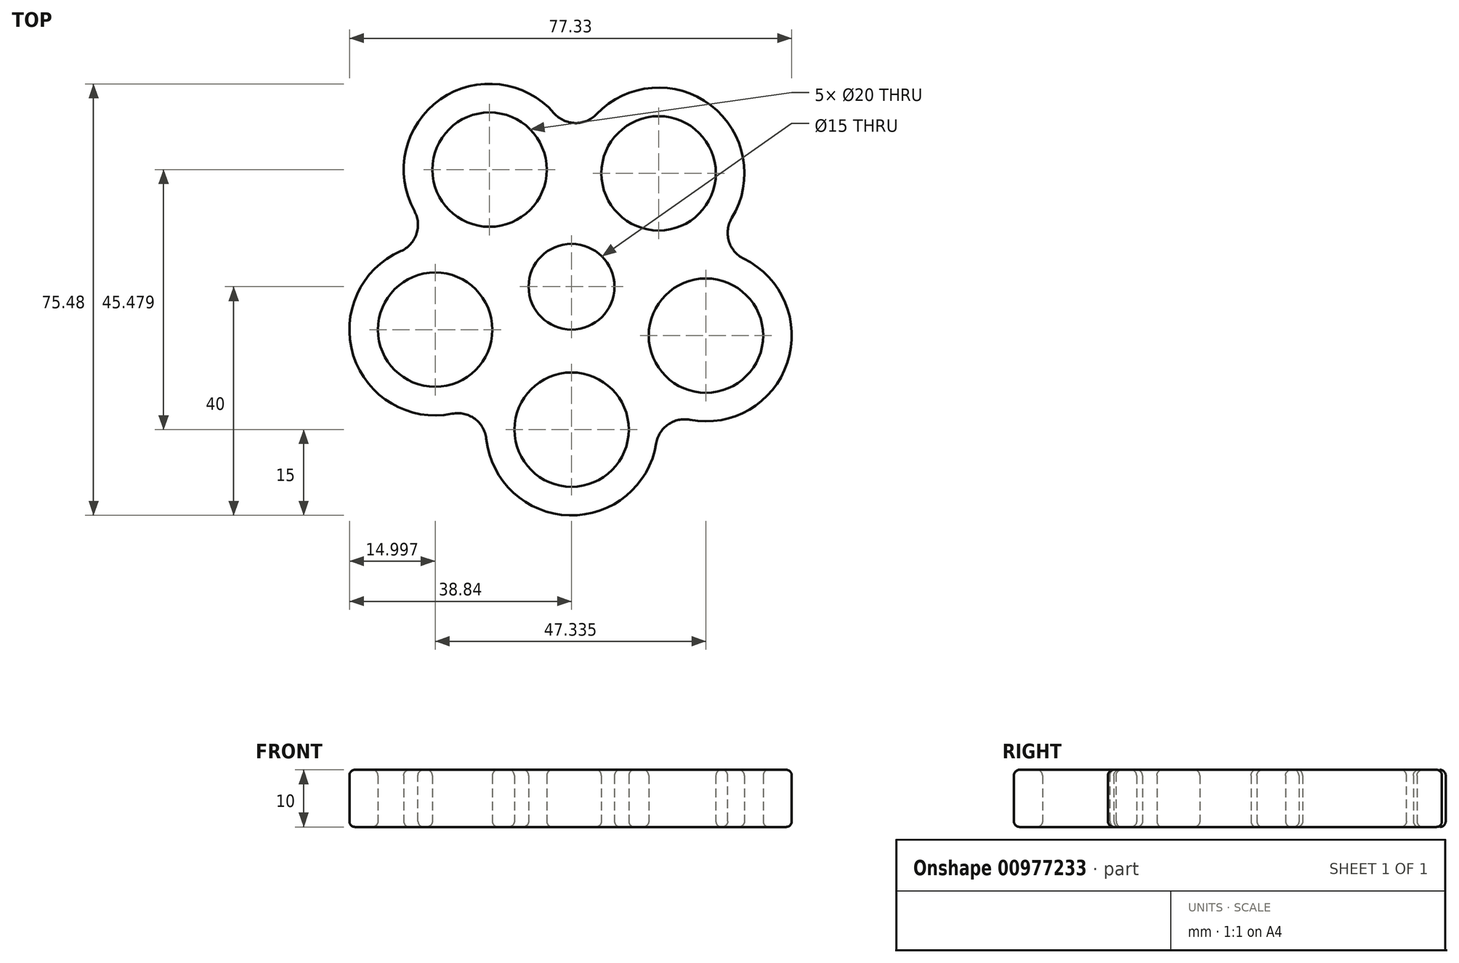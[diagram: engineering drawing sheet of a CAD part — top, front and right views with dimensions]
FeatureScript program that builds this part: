
annotation { "Feature Type Name" : "Feature", "Feature Type Description" : "" }
export const myFeature = defineFeature(function(context is Context, id is Id, definition is map)
    precondition{}
    {
        {
            var Q0;
            Q0=qCreatedBy(makeId("Top.planeOp"),FACE);
            var sketch = newSketch(context, id + "F0", { "sketchPlane" : qUnion([Q0])});
            skCircle(sketch, "E0", {"center": v(0, 0) * mm, "radius": 7.5 * mm});
            skCircle(sketch, "E1", {"center": v(0, 0) * mm, "radius": 15 * mm});
            skCircle(sketch, "E2", {"center": v(0, -25) * mm, "radius": 10 * mm});
            skCircle(sketch, "E3", {"center": v(0, -25) * mm, "radius": 15 * mm});
            skCircle(sketch, "E4.1.0", {"center": v(-23.84, -7.52) * mm, "radius": 15 * mm});
            skCircle(sketch, "E4.1.1", {"center": v(-23.84, -7.52) * mm, "radius": 10 * mm});
            skCircle(sketch, "E4.2.0", {"center": v(-14.34, 20.48) * mm, "radius": 15 * mm});
            skCircle(sketch, "E4.2.1", {"center": v(-14.34, 20.48) * mm, "radius": 10 * mm});
            skCircle(sketch, "E4.3.0", {"center": v(15.22, 19.83) * mm, "radius": 15 * mm});
            skCircle(sketch, "E4.3.1", {"center": v(15.22, 19.83) * mm, "radius": 10 * mm});
            skCircle(sketch, "E4.4.0", {"center": v(23.5, -8.55) * mm, "radius": 15 * mm});
            skCircle(sketch, "E4.4.1", {"center": v(23.5, -8.55) * mm, "radius": 10 * mm});
            skSolve(sketch);
        }
        {
            var Q0;
            Q0 = qSketchRegion(id + "F0", true);
            var Q1;
            {var subQ0=sQuery(id+"F0.wireOp",EDGE,"E1");var subQ1=makeQuery(id+"F0.imprint","INTERSECT",VERTEX,{"derivedFrom":[subQ0,sQuery(id+"F0.wireOp",EDGE,"E4.2.1")]});Q1=makeQuery(id+"F0.imprint","IMPRINT",FACE,{"disambiguationData":[TD([[makeQuery(id+"F0.imprint","IMPRINT",EDGE,{"disambiguationData":[TD([[subQ1,1.0]])],"derivedFrom":subQ0}),1.0]])]});}
            var Q2;
            {var subQ0=sQuery(id+"F0.wireOp",EDGE,"E1");var subQ1=makeQuery(id+"F0.imprint","INTERSECT",VERTEX,{"derivedFrom":[subQ0,sQuery(id+"F0.wireOp",EDGE,"E4.1.1")]});Q2=makeQuery(id+"F0.imprint","IMPRINT",FACE,{"disambiguationData":[TD([[makeQuery(id+"F0.imprint","IMPRINT",EDGE,{"disambiguationData":[TD([[subQ1,1.0]])],"derivedFrom":subQ0}),1.0]])]});}
            var Q3;
            Q3=makeQuery(id+"F0.imprint","IMPRINT",FACE,{"disambiguationData":[TD([[makeQuery(id+"F0.imprint","IMPRINT",EDGE,{"derivedFrom":sQuery(id+"F0.wireOp",EDGE,"E0")}),-1.0]])]});
            var Q4;
            {var subQ0=sQuery(id+"F0.wireOp",EDGE,"E1");var subQ1=makeQuery(id+"F0.imprint","INTERSECT",VERTEX,{"derivedFrom":[subQ0,sQuery(id+"F0.wireOp",EDGE,"E2")]});Q4=makeQuery(id+"F0.imprint","IMPRINT",FACE,{"disambiguationData":[TD([[makeQuery(id+"F0.imprint","IMPRINT",EDGE,{"disambiguationData":[TD([[subQ1,1.0]])],"derivedFrom":subQ0}),1.0]])]});}
            var Q5;
            {var subQ0=sQuery(id+"F0.wireOp",EDGE,"E1");var subQ1=makeQuery(id+"F0.imprint","INTERSECT",VERTEX,{"derivedFrom":[subQ0,sQuery(id+"F0.wireOp",EDGE,"E4.4.1")]});Q5=makeQuery(id+"F0.imprint","IMPRINT",FACE,{"disambiguationData":[TD([[makeQuery(id+"F0.imprint","IMPRINT",EDGE,{"disambiguationData":[TD([[subQ1,1.0]])],"derivedFrom":subQ0}),1.0]])]});}
            var Q6;
            {var subQ0=sQuery(id+"F0.wireOp",EDGE,"E1");var subQ1=makeQuery(id+"F0.imprint","INTERSECT",VERTEX,{"derivedFrom":[subQ0,sQuery(id+"F0.wireOp",EDGE,"E4.3.1")]});Q6=makeQuery(id+"F0.imprint","IMPRINT",FACE,{"disambiguationData":[TD([[makeQuery(id+"F0.imprint","IMPRINT",EDGE,{"disambiguationData":[TD([[subQ1,1.0]])],"derivedFrom":subQ0}),1.0]])]});}
            var Q7;
            {var subQ0=sQuery(id+"F0.wireOp",EDGE,"E4.3.0");var subQ1=sQuery(id+"F0.wireOp",EDGE,"E1");var subQ2=makeQuery(id+"F0.imprint","INTERSECT",VERTEX,{"disambiguationData":[OD(0.0)],"derivedFrom":[subQ1,subQ0]});Q7=makeQuery(id+"F0.imprint","IMPRINT",FACE,{"disambiguationData":[TD([[makeQuery(id+"F0.imprint","IMPRINT",EDGE,{"disambiguationData":[TD([[subQ2,1.0]])],"derivedFrom":subQ1}),-1.0]])]});}
            var Q8;
            {var subQ0=sQuery(id+"F0.wireOp",EDGE,"E4.3.0");var subQ1=sQuery(id+"F0.wireOp",EDGE,"E1");var subQ2=makeQuery(id+"F0.imprint","INTERSECT",VERTEX,{"disambiguationData":[OD(1.0)],"derivedFrom":[subQ1,subQ0]});Q8=makeQuery(id+"F0.imprint","IMPRINT",FACE,{"disambiguationData":[TD([[makeQuery(id+"F0.imprint","IMPRINT",EDGE,{"disambiguationData":[TD([[subQ2,-1.0]])],"derivedFrom":subQ1}),-1.0]])]});}
            var Q9;
            {var subQ0=sQuery(id+"F0.wireOp",EDGE,"E4.2.0");var subQ1=sQuery(id+"F0.wireOp",EDGE,"E1");var subQ2=makeQuery(id+"F0.imprint","INTERSECT",VERTEX,{"disambiguationData":[OD(1.0)],"derivedFrom":[subQ1,subQ0]});Q9=makeQuery(id+"F0.imprint","IMPRINT",FACE,{"disambiguationData":[TD([[makeQuery(id+"F0.imprint","IMPRINT",EDGE,{"disambiguationData":[TD([[subQ2,-1.0]])],"derivedFrom":subQ1}),-1.0]])]});}
            var Q10;
            {var subQ0=sQuery(id+"F0.wireOp",EDGE,"E4.1.0");var subQ1=sQuery(id+"F0.wireOp",EDGE,"E1");var subQ2=makeQuery(id+"F0.imprint","INTERSECT",VERTEX,{"disambiguationData":[OD(1.0)],"derivedFrom":[subQ1,subQ0]});Q10=makeQuery(id+"F0.imprint","IMPRINT",FACE,{"disambiguationData":[TD([[makeQuery(id+"F0.imprint","IMPRINT",EDGE,{"disambiguationData":[TD([[subQ2,-1.0]])],"derivedFrom":subQ1}),-1.0]])]});}
            var Q11;
            {var subQ0=sQuery(id+"F0.wireOp",EDGE,"E3");var subQ1=sQuery(id+"F0.wireOp",EDGE,"E1");var subQ2=makeQuery(id+"F0.imprint","INTERSECT",VERTEX,{"disambiguationData":[OD(1.0)],"derivedFrom":[subQ1,subQ0]});Q11=makeQuery(id+"F0.imprint","IMPRINT",FACE,{"disambiguationData":[TD([[makeQuery(id+"F0.imprint","IMPRINT",EDGE,{"disambiguationData":[TD([[subQ2,-1.0]])],"derivedFrom":subQ1}),-1.0]])]});}
            extrude(context, id + "F1", {"entities" : qUnion([Q0, Q1, Q2, Q3, Q4, Q5, Q6, Q7, Q8, Q9, Q10, Q11]), "depth" : 10 * mm, "offsetDistance" : 25 * mm});
        }
        {
            var Q0;
            Q0=makeQuery(id+"F1.opExtrude","SWEPT_EDGE",EDGE,{"disambiguationData":[OSD([sQuery(id+"F0.wireOp",EDGE,"E3"),sQuery(id+"F0.wireOp",EDGE,"E4.4.0")])]});
            var Q1;
            Q1=makeQuery(id+"F1.opExtrude","SWEPT_EDGE",EDGE,{"disambiguationData":[OSD([sQuery(id+"F0.wireOp",EDGE,"E4.3.0"),sQuery(id+"F0.wireOp",EDGE,"E4.4.0")])]});
            var Q2;
            Q2=makeQuery(id+"F1.opExtrude","SWEPT_EDGE",EDGE,{"disambiguationData":[OSD([sQuery(id+"F0.wireOp",EDGE,"E4.2.0"),sQuery(id+"F0.wireOp",EDGE,"E4.3.0")])]});
            var Q3;
            Q3=makeQuery(id+"F1.opExtrude","SWEPT_EDGE",EDGE,{"disambiguationData":[OSD([sQuery(id+"F0.wireOp",EDGE,"E4.1.0"),sQuery(id+"F0.wireOp",EDGE,"E4.2.0")])]});
            var Q4;
            Q4=makeQuery(id+"F1.opExtrude","SWEPT_EDGE",EDGE,{"disambiguationData":[OSD([sQuery(id+"F0.wireOp",EDGE,"E3"),sQuery(id+"F0.wireOp",EDGE,"E4.1.0")])]});
            fillet(context, id + "F2", {"entities" : qUnion([Q0, Q1, Q2, Q3, Q4]), "radius" : 5 * mm, "tangentPropagation" : true, "allowEdgeOverflow" : false});
        }
        {
            var Q0;
            {var subQ0=sQuery(id+"F0.wireOp",EDGE,"E4.2.0");var subQ1=sQuery(id+"F0.wireOp",EDGE,"E4.1.0");Q0=makeQuery(id+"F2.opFillet","BLEND_EDGE",EDGE,{"blendedFrom":[makeQuery(id+"F1.opExtrude","SWEPT_EDGE",EDGE,{"disambiguationData":[OSD([subQ1,subQ0])]}),makeQuery(id+"F1.opExtrude","CAP_FACE",FACE,{"disambiguationData":[OSD([sQuery(id+"F0.wireOp",EDGE,"E0"),sQuery(id+"F0.wireOp",EDGE,"E2"),sQuery(id+"F0.wireOp",EDGE,"E3"),subQ1,sQuery(id+"F0.wireOp",EDGE,"E4.1.1"),subQ0,sQuery(id+"F0.wireOp",EDGE,"E4.2.1"),sQuery(id+"F0.wireOp",EDGE,"E4.3.0"),sQuery(id+"F0.wireOp",EDGE,"E4.3.1"),sQuery(id+"F0.wireOp",EDGE,"E4.4.0"),sQuery(id+"F0.wireOp",EDGE,"E4.4.1")])],"isStart":true})],"blendedInto":[makeQuery(id+"F1.opExtrude","CAP_FACE",FACE,{"disambiguationData":[OSD([sQuery(id+"F0.wireOp",EDGE,"E0"),sQuery(id+"F0.wireOp",EDGE,"E2"),sQuery(id+"F0.wireOp",EDGE,"E3"),subQ1,sQuery(id+"F0.wireOp",EDGE,"E4.1.1"),subQ0,sQuery(id+"F0.wireOp",EDGE,"E4.2.1"),sQuery(id+"F0.wireOp",EDGE,"E4.3.0"),sQuery(id+"F0.wireOp",EDGE,"E4.3.1"),sQuery(id+"F0.wireOp",EDGE,"E4.4.0"),sQuery(id+"F0.wireOp",EDGE,"E4.4.1")])],"isStart":true})]});}
            var Q1;
            Q1=makeQuery(id+"F1.opExtrude","CAP_EDGE",EDGE,{"disambiguationData":[OSD([sQuery(id+"F0.wireOp",EDGE,"E4.1.1")])],"isStart":true});
            var Q2;
            {var subQ0=sQuery(id+"F0.wireOp",EDGE,"E4.1.0");var subQ1=sQuery(id+"F0.wireOp",EDGE,"E3");Q2=makeQuery(id+"F2.opFillet","BLEND_EDGE",EDGE,{"blendedFrom":[makeQuery(id+"F1.opExtrude","SWEPT_EDGE",EDGE,{"disambiguationData":[OSD([subQ1,subQ0])]}),makeQuery(id+"F1.opExtrude","CAP_FACE",FACE,{"disambiguationData":[OSD([sQuery(id+"F0.wireOp",EDGE,"E0"),sQuery(id+"F0.wireOp",EDGE,"E2"),subQ1,subQ0,sQuery(id+"F0.wireOp",EDGE,"E4.1.1"),sQuery(id+"F0.wireOp",EDGE,"E4.2.0"),sQuery(id+"F0.wireOp",EDGE,"E4.2.1"),sQuery(id+"F0.wireOp",EDGE,"E4.3.0"),sQuery(id+"F0.wireOp",EDGE,"E4.3.1"),sQuery(id+"F0.wireOp",EDGE,"E4.4.0"),sQuery(id+"F0.wireOp",EDGE,"E4.4.1")])],"isStart":false})],"blendedInto":[makeQuery(id+"F1.opExtrude","CAP_FACE",FACE,{"disambiguationData":[OSD([sQuery(id+"F0.wireOp",EDGE,"E0"),sQuery(id+"F0.wireOp",EDGE,"E2"),subQ1,subQ0,sQuery(id+"F0.wireOp",EDGE,"E4.1.1"),sQuery(id+"F0.wireOp",EDGE,"E4.2.0"),sQuery(id+"F0.wireOp",EDGE,"E4.2.1"),sQuery(id+"F0.wireOp",EDGE,"E4.3.0"),sQuery(id+"F0.wireOp",EDGE,"E4.3.1"),sQuery(id+"F0.wireOp",EDGE,"E4.4.0"),sQuery(id+"F0.wireOp",EDGE,"E4.4.1")])],"isStart":false})]});}
            var Q3;
            {var subQ0=sQuery(id+"F0.wireOp",EDGE,"E4.1.0");var subQ1=sQuery(id+"F0.wireOp",EDGE,"E3");Q3=makeQuery(id+"F2.opFillet","BLEND_EDGE",EDGE,{"blendedFrom":[makeQuery(id+"F1.opExtrude","SWEPT_EDGE",EDGE,{"disambiguationData":[OSD([subQ1,subQ0])]}),makeQuery(id+"F1.opExtrude","CAP_FACE",FACE,{"disambiguationData":[OSD([sQuery(id+"F0.wireOp",EDGE,"E0"),sQuery(id+"F0.wireOp",EDGE,"E2"),subQ1,subQ0,sQuery(id+"F0.wireOp",EDGE,"E4.1.1"),sQuery(id+"F0.wireOp",EDGE,"E4.2.0"),sQuery(id+"F0.wireOp",EDGE,"E4.2.1"),sQuery(id+"F0.wireOp",EDGE,"E4.3.0"),sQuery(id+"F0.wireOp",EDGE,"E4.3.1"),sQuery(id+"F0.wireOp",EDGE,"E4.4.0"),sQuery(id+"F0.wireOp",EDGE,"E4.4.1")])],"isStart":true})],"blendedInto":[makeQuery(id+"F1.opExtrude","CAP_FACE",FACE,{"disambiguationData":[OSD([sQuery(id+"F0.wireOp",EDGE,"E0"),sQuery(id+"F0.wireOp",EDGE,"E2"),subQ1,subQ0,sQuery(id+"F0.wireOp",EDGE,"E4.1.1"),sQuery(id+"F0.wireOp",EDGE,"E4.2.0"),sQuery(id+"F0.wireOp",EDGE,"E4.2.1"),sQuery(id+"F0.wireOp",EDGE,"E4.3.0"),sQuery(id+"F0.wireOp",EDGE,"E4.3.1"),sQuery(id+"F0.wireOp",EDGE,"E4.4.0"),sQuery(id+"F0.wireOp",EDGE,"E4.4.1")])],"isStart":true})]});}
            var Q4;
            Q4=makeQuery(id+"F1.opExtrude","CAP_EDGE",EDGE,{"disambiguationData":[OSD([sQuery(id+"F0.wireOp",EDGE,"E0")])],"isStart":true});
            var Q5;
            Q5=makeQuery(id+"F1.opExtrude","CAP_EDGE",EDGE,{"disambiguationData":[OSD([sQuery(id+"F0.wireOp",EDGE,"E2")])],"isStart":true});
            var Q6;
            Q6=makeQuery(id+"F1.opExtrude","CAP_EDGE",EDGE,{"disambiguationData":[OSD([sQuery(id+"F0.wireOp",EDGE,"E2")])],"isStart":false});
            var Q7;
            {var subQ0=sQuery(id+"F0.wireOp",EDGE,"E4.4.0");var subQ1=sQuery(id+"F0.wireOp",EDGE,"E3");Q7=makeQuery(id+"F2.opFillet","BLEND_EDGE",EDGE,{"blendedFrom":[makeQuery(id+"F1.opExtrude","SWEPT_EDGE",EDGE,{"disambiguationData":[OSD([subQ1,subQ0])]}),makeQuery(id+"F1.opExtrude","CAP_FACE",FACE,{"disambiguationData":[OSD([sQuery(id+"F0.wireOp",EDGE,"E0"),sQuery(id+"F0.wireOp",EDGE,"E2"),subQ1,sQuery(id+"F0.wireOp",EDGE,"E4.1.0"),sQuery(id+"F0.wireOp",EDGE,"E4.1.1"),sQuery(id+"F0.wireOp",EDGE,"E4.2.0"),sQuery(id+"F0.wireOp",EDGE,"E4.2.1"),sQuery(id+"F0.wireOp",EDGE,"E4.3.0"),sQuery(id+"F0.wireOp",EDGE,"E4.3.1"),subQ0,sQuery(id+"F0.wireOp",EDGE,"E4.4.1")])],"isStart":true})],"blendedInto":[makeQuery(id+"F1.opExtrude","CAP_FACE",FACE,{"disambiguationData":[OSD([sQuery(id+"F0.wireOp",EDGE,"E0"),sQuery(id+"F0.wireOp",EDGE,"E2"),subQ1,sQuery(id+"F0.wireOp",EDGE,"E4.1.0"),sQuery(id+"F0.wireOp",EDGE,"E4.1.1"),sQuery(id+"F0.wireOp",EDGE,"E4.2.0"),sQuery(id+"F0.wireOp",EDGE,"E4.2.1"),sQuery(id+"F0.wireOp",EDGE,"E4.3.0"),sQuery(id+"F0.wireOp",EDGE,"E4.3.1"),subQ0,sQuery(id+"F0.wireOp",EDGE,"E4.4.1")])],"isStart":true})]});}
            var Q8;
            Q8=makeQuery(id+"F1.opExtrude","CAP_EDGE",EDGE,{"disambiguationData":[OSD([sQuery(id+"F0.wireOp",EDGE,"E4.2.1")])],"isStart":true});
            var Q9;
            Q9=makeQuery(id+"F1.opExtrude","CAP_EDGE",EDGE,{"disambiguationData":[OSD([sQuery(id+"F0.wireOp",EDGE,"E4.2.1")])],"isStart":false});
            var Q10;
            Q10=makeQuery(id+"F1.opExtrude","CAP_EDGE",EDGE,{"disambiguationData":[OSD([sQuery(id+"F0.wireOp",EDGE,"E4.3.1")])],"isStart":true});
            var Q11;
            Q11=makeQuery(id+"F1.opExtrude","CAP_EDGE",EDGE,{"disambiguationData":[OSD([sQuery(id+"F0.wireOp",EDGE,"E4.3.1")])],"isStart":false});
            var Q12;
            Q12=makeQuery(id+"F1.opExtrude","CAP_EDGE",EDGE,{"disambiguationData":[OSD([sQuery(id+"F0.wireOp",EDGE,"E4.4.1")])],"isStart":true});
            var Q13;
            Q13=makeQuery(id+"F1.opExtrude","CAP_EDGE",EDGE,{"disambiguationData":[OSD([sQuery(id+"F0.wireOp",EDGE,"E4.4.1")])],"isStart":false});
            var Q14;
            {var subQ0=sQuery(id+"F0.wireOp",EDGE,"E4.3.0");var subQ1=sQuery(id+"F0.wireOp",EDGE,"E4.2.0");Q14=makeQuery(id+"F2.opFillet","BLEND_EDGE",EDGE,{"blendedFrom":[makeQuery(id+"F1.opExtrude","SWEPT_EDGE",EDGE,{"disambiguationData":[OSD([subQ1,subQ0])]}),makeQuery(id+"F1.opExtrude","CAP_FACE",FACE,{"disambiguationData":[OSD([sQuery(id+"F0.wireOp",EDGE,"E0"),sQuery(id+"F0.wireOp",EDGE,"E2"),sQuery(id+"F0.wireOp",EDGE,"E3"),sQuery(id+"F0.wireOp",EDGE,"E4.1.0"),sQuery(id+"F0.wireOp",EDGE,"E4.1.1"),subQ1,sQuery(id+"F0.wireOp",EDGE,"E4.2.1"),subQ0,sQuery(id+"F0.wireOp",EDGE,"E4.3.1"),sQuery(id+"F0.wireOp",EDGE,"E4.4.0"),sQuery(id+"F0.wireOp",EDGE,"E4.4.1")])],"isStart":true})],"blendedInto":[makeQuery(id+"F1.opExtrude","CAP_FACE",FACE,{"disambiguationData":[OSD([sQuery(id+"F0.wireOp",EDGE,"E0"),sQuery(id+"F0.wireOp",EDGE,"E2"),sQuery(id+"F0.wireOp",EDGE,"E3"),sQuery(id+"F0.wireOp",EDGE,"E4.1.0"),sQuery(id+"F0.wireOp",EDGE,"E4.1.1"),subQ1,sQuery(id+"F0.wireOp",EDGE,"E4.2.1"),subQ0,sQuery(id+"F0.wireOp",EDGE,"E4.3.1"),sQuery(id+"F0.wireOp",EDGE,"E4.4.0"),sQuery(id+"F0.wireOp",EDGE,"E4.4.1")])],"isStart":true})]});}
            var Q15;
            Q15=makeQuery(id+"F1.opExtrude","CAP_EDGE",EDGE,{"disambiguationData":[OSD([sQuery(id+"F0.wireOp",EDGE,"E4.4.0")])],"isStart":false});
            var Q16;
            {var subQ0=sQuery(id+"F0.wireOp",EDGE,"E4.4.0");var subQ1=sQuery(id+"F0.wireOp",EDGE,"E4.3.0");Q16=makeQuery(id+"F2.opFillet","BLEND_EDGE",EDGE,{"blendedFrom":[makeQuery(id+"F1.opExtrude","SWEPT_EDGE",EDGE,{"disambiguationData":[OSD([subQ1,subQ0])]}),makeQuery(id+"F1.opExtrude","CAP_FACE",FACE,{"disambiguationData":[OSD([sQuery(id+"F0.wireOp",EDGE,"E0"),sQuery(id+"F0.wireOp",EDGE,"E2"),sQuery(id+"F0.wireOp",EDGE,"E3"),sQuery(id+"F0.wireOp",EDGE,"E4.1.0"),sQuery(id+"F0.wireOp",EDGE,"E4.1.1"),sQuery(id+"F0.wireOp",EDGE,"E4.2.0"),sQuery(id+"F0.wireOp",EDGE,"E4.2.1"),subQ1,sQuery(id+"F0.wireOp",EDGE,"E4.3.1"),subQ0,sQuery(id+"F0.wireOp",EDGE,"E4.4.1")])],"isStart":true})],"blendedInto":[makeQuery(id+"F1.opExtrude","CAP_FACE",FACE,{"disambiguationData":[OSD([sQuery(id+"F0.wireOp",EDGE,"E0"),sQuery(id+"F0.wireOp",EDGE,"E2"),sQuery(id+"F0.wireOp",EDGE,"E3"),sQuery(id+"F0.wireOp",EDGE,"E4.1.0"),sQuery(id+"F0.wireOp",EDGE,"E4.1.1"),sQuery(id+"F0.wireOp",EDGE,"E4.2.0"),sQuery(id+"F0.wireOp",EDGE,"E4.2.1"),subQ1,sQuery(id+"F0.wireOp",EDGE,"E4.3.1"),subQ0,sQuery(id+"F0.wireOp",EDGE,"E4.4.1")])],"isStart":true})]});}
            var Q17;
            Q17=makeQuery(id+"F1.opExtrude","CAP_EDGE",EDGE,{"disambiguationData":[OSD([sQuery(id+"F0.wireOp",EDGE,"E3")])],"isStart":true});
            var Q18;
            Q18=makeQuery(id+"F1.opExtrude","CAP_EDGE",EDGE,{"disambiguationData":[OSD([sQuery(id+"F0.wireOp",EDGE,"E3")])],"isStart":false});
            var Q19;
            Q19=makeQuery(id+"F1.opExtrude","CAP_EDGE",EDGE,{"disambiguationData":[OSD([sQuery(id+"F0.wireOp",EDGE,"E4.1.0")])],"isStart":true});
            var Q20;
            Q20=makeQuery(id+"F1.opExtrude","CAP_EDGE",EDGE,{"disambiguationData":[OSD([sQuery(id+"F0.wireOp",EDGE,"E4.1.0")])],"isStart":false});
            var Q21;
            Q21=makeQuery(id+"F1.opExtrude","CAP_EDGE",EDGE,{"disambiguationData":[OSD([sQuery(id+"F0.wireOp",EDGE,"E4.2.0")])],"isStart":true});
            var Q22;
            Q22=makeQuery(id+"F1.opExtrude","CAP_EDGE",EDGE,{"disambiguationData":[OSD([sQuery(id+"F0.wireOp",EDGE,"E4.2.0")])],"isStart":false});
            var Q23;
            Q23=makeQuery(id+"F1.opExtrude","CAP_EDGE",EDGE,{"disambiguationData":[OSD([sQuery(id+"F0.wireOp",EDGE,"E4.3.0")])],"isStart":true});
            var Q24;
            Q24=makeQuery(id+"F1.opExtrude","CAP_EDGE",EDGE,{"disambiguationData":[OSD([sQuery(id+"F0.wireOp",EDGE,"E4.4.0")])],"isStart":true});
            var Q25;
            Q25=makeQuery(id+"F1.opExtrude","CAP_EDGE",EDGE,{"disambiguationData":[OSD([sQuery(id+"F0.wireOp",EDGE,"E4.1.1")])],"isStart":false});
            var Q26;
            {var subQ0=sQuery(id+"F0.wireOp",EDGE,"E4.1.0");Q26=makeQuery(id+"F2.opFillet","BLEND_EDGE",EDGE,{"blendedFrom":[makeQuery(id+"F1.opExtrude","SWEPT_EDGE",EDGE,{"disambiguationData":[OSD([sQuery(id+"F0.wireOp",EDGE,"E3"),subQ0])]}),makeQuery(id+"F1.opExtrude","SWEPT_FACE",FACE,{"disambiguationData":[OSD([subQ0])]})],"blendedInto":[makeQuery(id+"F1.opExtrude","SWEPT_FACE",FACE,{"disambiguationData":[OSD([subQ0])]})]});}
            var Q27;
            {var subQ0=sQuery(id+"F0.wireOp",EDGE,"E3");Q27=makeQuery(id+"F2.opFillet","BLEND_EDGE",EDGE,{"blendedFrom":[makeQuery(id+"F1.opExtrude","SWEPT_EDGE",EDGE,{"disambiguationData":[OSD([subQ0,sQuery(id+"F0.wireOp",EDGE,"E4.1.0")])]}),makeQuery(id+"F1.opExtrude","SWEPT_FACE",FACE,{"disambiguationData":[OSD([subQ0])]})],"blendedInto":[makeQuery(id+"F1.opExtrude","SWEPT_FACE",FACE,{"disambiguationData":[OSD([subQ0])]})]});}
            var Q28;
            {var subQ0=sQuery(id+"F0.wireOp",EDGE,"E4.4.0");Q28=makeQuery(id+"F2.opFillet","BLEND_EDGE",EDGE,{"blendedFrom":[makeQuery(id+"F1.opExtrude","SWEPT_EDGE",EDGE,{"disambiguationData":[OSD([sQuery(id+"F0.wireOp",EDGE,"E3"),subQ0])]}),makeQuery(id+"F1.opExtrude","SWEPT_FACE",FACE,{"disambiguationData":[OSD([subQ0])]})],"blendedInto":[makeQuery(id+"F1.opExtrude","SWEPT_FACE",FACE,{"disambiguationData":[OSD([subQ0])]})]});}
            var Q29;
            {var subQ0=sQuery(id+"F0.wireOp",EDGE,"E3");Q29=makeQuery(id+"F2.opFillet","BLEND_EDGE",EDGE,{"blendedFrom":[makeQuery(id+"F1.opExtrude","SWEPT_EDGE",EDGE,{"disambiguationData":[OSD([subQ0,sQuery(id+"F0.wireOp",EDGE,"E4.4.0")])]}),makeQuery(id+"F1.opExtrude","SWEPT_FACE",FACE,{"disambiguationData":[OSD([subQ0])]})],"blendedInto":[makeQuery(id+"F1.opExtrude","SWEPT_FACE",FACE,{"disambiguationData":[OSD([subQ0])]})]});}
            var Q30;
            Q30=makeQuery(id+"F1.opExtrude","CAP_EDGE",EDGE,{"disambiguationData":[OSD([sQuery(id+"F0.wireOp",EDGE,"E0")])],"isStart":false});
            var Q31;
            {var subQ0=sQuery(id+"F0.wireOp",EDGE,"E4.4.0");var subQ1=sQuery(id+"F0.wireOp",EDGE,"E3");Q31=makeQuery(id+"F2.opFillet","BLEND_EDGE",EDGE,{"blendedFrom":[makeQuery(id+"F1.opExtrude","SWEPT_EDGE",EDGE,{"disambiguationData":[OSD([subQ1,subQ0])]}),makeQuery(id+"F1.opExtrude","CAP_FACE",FACE,{"disambiguationData":[OSD([sQuery(id+"F0.wireOp",EDGE,"E0"),sQuery(id+"F0.wireOp",EDGE,"E2"),subQ1,sQuery(id+"F0.wireOp",EDGE,"E4.1.0"),sQuery(id+"F0.wireOp",EDGE,"E4.1.1"),sQuery(id+"F0.wireOp",EDGE,"E4.2.0"),sQuery(id+"F0.wireOp",EDGE,"E4.2.1"),sQuery(id+"F0.wireOp",EDGE,"E4.3.0"),sQuery(id+"F0.wireOp",EDGE,"E4.3.1"),subQ0,sQuery(id+"F0.wireOp",EDGE,"E4.4.1")])],"isStart":false})],"blendedInto":[makeQuery(id+"F1.opExtrude","CAP_FACE",FACE,{"disambiguationData":[OSD([sQuery(id+"F0.wireOp",EDGE,"E0"),sQuery(id+"F0.wireOp",EDGE,"E2"),subQ1,sQuery(id+"F0.wireOp",EDGE,"E4.1.0"),sQuery(id+"F0.wireOp",EDGE,"E4.1.1"),sQuery(id+"F0.wireOp",EDGE,"E4.2.0"),sQuery(id+"F0.wireOp",EDGE,"E4.2.1"),sQuery(id+"F0.wireOp",EDGE,"E4.3.0"),sQuery(id+"F0.wireOp",EDGE,"E4.3.1"),subQ0,sQuery(id+"F0.wireOp",EDGE,"E4.4.1")])],"isStart":false})]});}
            var Q32;
            {var subQ0=sQuery(id+"F0.wireOp",EDGE,"E4.3.0");Q32=makeQuery(id+"F2.opFillet","BLEND_EDGE",EDGE,{"blendedFrom":[makeQuery(id+"F1.opExtrude","SWEPT_EDGE",EDGE,{"disambiguationData":[OSD([sQuery(id+"F0.wireOp",EDGE,"E4.2.0"),subQ0])]}),makeQuery(id+"F1.opExtrude","SWEPT_FACE",FACE,{"disambiguationData":[OSD([subQ0])]})],"blendedInto":[makeQuery(id+"F1.opExtrude","SWEPT_FACE",FACE,{"disambiguationData":[OSD([subQ0])]})]});}
            var Q33;
            {var subQ0=sQuery(id+"F0.wireOp",EDGE,"E4.2.0");Q33=makeQuery(id+"F2.opFillet","BLEND_EDGE",EDGE,{"blendedFrom":[makeQuery(id+"F1.opExtrude","SWEPT_EDGE",EDGE,{"disambiguationData":[OSD([subQ0,sQuery(id+"F0.wireOp",EDGE,"E4.3.0")])]}),makeQuery(id+"F1.opExtrude","SWEPT_FACE",FACE,{"disambiguationData":[OSD([subQ0])]})],"blendedInto":[makeQuery(id+"F1.opExtrude","SWEPT_FACE",FACE,{"disambiguationData":[OSD([subQ0])]})]});}
            var Q34;
            {var subQ0=sQuery(id+"F0.wireOp",EDGE,"E4.3.0");var subQ1=sQuery(id+"F0.wireOp",EDGE,"E4.2.0");Q34=makeQuery(id+"F2.opFillet","BLEND_EDGE",EDGE,{"blendedFrom":[makeQuery(id+"F1.opExtrude","SWEPT_EDGE",EDGE,{"disambiguationData":[OSD([subQ1,subQ0])]}),makeQuery(id+"F1.opExtrude","CAP_FACE",FACE,{"disambiguationData":[OSD([sQuery(id+"F0.wireOp",EDGE,"E0"),sQuery(id+"F0.wireOp",EDGE,"E2"),sQuery(id+"F0.wireOp",EDGE,"E3"),sQuery(id+"F0.wireOp",EDGE,"E4.1.0"),sQuery(id+"F0.wireOp",EDGE,"E4.1.1"),subQ1,sQuery(id+"F0.wireOp",EDGE,"E4.2.1"),subQ0,sQuery(id+"F0.wireOp",EDGE,"E4.3.1"),sQuery(id+"F0.wireOp",EDGE,"E4.4.0"),sQuery(id+"F0.wireOp",EDGE,"E4.4.1")])],"isStart":false})],"blendedInto":[makeQuery(id+"F1.opExtrude","CAP_FACE",FACE,{"disambiguationData":[OSD([sQuery(id+"F0.wireOp",EDGE,"E0"),sQuery(id+"F0.wireOp",EDGE,"E2"),sQuery(id+"F0.wireOp",EDGE,"E3"),sQuery(id+"F0.wireOp",EDGE,"E4.1.0"),sQuery(id+"F0.wireOp",EDGE,"E4.1.1"),subQ1,sQuery(id+"F0.wireOp",EDGE,"E4.2.1"),subQ0,sQuery(id+"F0.wireOp",EDGE,"E4.3.1"),sQuery(id+"F0.wireOp",EDGE,"E4.4.0"),sQuery(id+"F0.wireOp",EDGE,"E4.4.1")])],"isStart":false})]});}
            var Q35;
            {var subQ0=sQuery(id+"F0.wireOp",EDGE,"E4.2.0");var subQ1=sQuery(id+"F0.wireOp",EDGE,"E4.1.0");Q35=makeQuery(id+"F2.opFillet","BLEND_EDGE",EDGE,{"blendedFrom":[makeQuery(id+"F1.opExtrude","SWEPT_EDGE",EDGE,{"disambiguationData":[OSD([subQ1,subQ0])]}),makeQuery(id+"F1.opExtrude","CAP_FACE",FACE,{"disambiguationData":[OSD([sQuery(id+"F0.wireOp",EDGE,"E0"),sQuery(id+"F0.wireOp",EDGE,"E2"),sQuery(id+"F0.wireOp",EDGE,"E3"),subQ1,sQuery(id+"F0.wireOp",EDGE,"E4.1.1"),subQ0,sQuery(id+"F0.wireOp",EDGE,"E4.2.1"),sQuery(id+"F0.wireOp",EDGE,"E4.3.0"),sQuery(id+"F0.wireOp",EDGE,"E4.3.1"),sQuery(id+"F0.wireOp",EDGE,"E4.4.0"),sQuery(id+"F0.wireOp",EDGE,"E4.4.1")])],"isStart":false})],"blendedInto":[makeQuery(id+"F1.opExtrude","CAP_FACE",FACE,{"disambiguationData":[OSD([sQuery(id+"F0.wireOp",EDGE,"E0"),sQuery(id+"F0.wireOp",EDGE,"E2"),sQuery(id+"F0.wireOp",EDGE,"E3"),subQ1,sQuery(id+"F0.wireOp",EDGE,"E4.1.1"),subQ0,sQuery(id+"F0.wireOp",EDGE,"E4.2.1"),sQuery(id+"F0.wireOp",EDGE,"E4.3.0"),sQuery(id+"F0.wireOp",EDGE,"E4.3.1"),sQuery(id+"F0.wireOp",EDGE,"E4.4.0"),sQuery(id+"F0.wireOp",EDGE,"E4.4.1")])],"isStart":false})]});}
            var Q36;
            {var subQ0=sQuery(id+"F0.wireOp",EDGE,"E4.1.0");Q36=makeQuery(id+"F2.opFillet","BLEND_EDGE",EDGE,{"blendedFrom":[makeQuery(id+"F1.opExtrude","SWEPT_EDGE",EDGE,{"disambiguationData":[OSD([subQ0,sQuery(id+"F0.wireOp",EDGE,"E4.2.0")])]}),makeQuery(id+"F1.opExtrude","SWEPT_FACE",FACE,{"disambiguationData":[OSD([subQ0])]})],"blendedInto":[makeQuery(id+"F1.opExtrude","SWEPT_FACE",FACE,{"disambiguationData":[OSD([subQ0])]})]});}
            var Q37;
            {var subQ0=sQuery(id+"F0.wireOp",EDGE,"E4.2.0");Q37=makeQuery(id+"F2.opFillet","BLEND_EDGE",EDGE,{"blendedFrom":[makeQuery(id+"F1.opExtrude","SWEPT_EDGE",EDGE,{"disambiguationData":[OSD([sQuery(id+"F0.wireOp",EDGE,"E4.1.0"),subQ0])]}),makeQuery(id+"F1.opExtrude","SWEPT_FACE",FACE,{"disambiguationData":[OSD([subQ0])]})],"blendedInto":[makeQuery(id+"F1.opExtrude","SWEPT_FACE",FACE,{"disambiguationData":[OSD([subQ0])]})]});}
            var Q38;
            {var subQ0=sQuery(id+"F0.wireOp",EDGE,"E4.4.0");var subQ1=sQuery(id+"F0.wireOp",EDGE,"E4.3.0");Q38=makeQuery(id+"F2.opFillet","BLEND_EDGE",EDGE,{"blendedFrom":[makeQuery(id+"F1.opExtrude","SWEPT_EDGE",EDGE,{"disambiguationData":[OSD([subQ1,subQ0])]}),makeQuery(id+"F1.opExtrude","CAP_FACE",FACE,{"disambiguationData":[OSD([sQuery(id+"F0.wireOp",EDGE,"E0"),sQuery(id+"F0.wireOp",EDGE,"E2"),sQuery(id+"F0.wireOp",EDGE,"E3"),sQuery(id+"F0.wireOp",EDGE,"E4.1.0"),sQuery(id+"F0.wireOp",EDGE,"E4.1.1"),sQuery(id+"F0.wireOp",EDGE,"E4.2.0"),sQuery(id+"F0.wireOp",EDGE,"E4.2.1"),subQ1,sQuery(id+"F0.wireOp",EDGE,"E4.3.1"),subQ0,sQuery(id+"F0.wireOp",EDGE,"E4.4.1")])],"isStart":false})],"blendedInto":[makeQuery(id+"F1.opExtrude","CAP_FACE",FACE,{"disambiguationData":[OSD([sQuery(id+"F0.wireOp",EDGE,"E0"),sQuery(id+"F0.wireOp",EDGE,"E2"),sQuery(id+"F0.wireOp",EDGE,"E3"),sQuery(id+"F0.wireOp",EDGE,"E4.1.0"),sQuery(id+"F0.wireOp",EDGE,"E4.1.1"),sQuery(id+"F0.wireOp",EDGE,"E4.2.0"),sQuery(id+"F0.wireOp",EDGE,"E4.2.1"),subQ1,sQuery(id+"F0.wireOp",EDGE,"E4.3.1"),subQ0,sQuery(id+"F0.wireOp",EDGE,"E4.4.1")])],"isStart":false})]});}
            var Q39;
            Q39=makeQuery(id+"F1.opExtrude","CAP_EDGE",EDGE,{"disambiguationData":[OSD([sQuery(id+"F0.wireOp",EDGE,"E4.3.0")])],"isStart":false});
            var Q40;
            {var subQ0=sQuery(id+"F0.wireOp",EDGE,"E4.3.0");Q40=makeQuery(id+"F2.opFillet","BLEND_EDGE",EDGE,{"blendedFrom":[makeQuery(id+"F1.opExtrude","SWEPT_EDGE",EDGE,{"disambiguationData":[OSD([subQ0,sQuery(id+"F0.wireOp",EDGE,"E4.4.0")])]}),makeQuery(id+"F1.opExtrude","SWEPT_FACE",FACE,{"disambiguationData":[OSD([subQ0])]})],"blendedInto":[makeQuery(id+"F1.opExtrude","SWEPT_FACE",FACE,{"disambiguationData":[OSD([subQ0])]})]});}
            var Q41;
            {var subQ0=sQuery(id+"F0.wireOp",EDGE,"E4.4.0");Q41=makeQuery(id+"F2.opFillet","BLEND_EDGE",EDGE,{"blendedFrom":[makeQuery(id+"F1.opExtrude","SWEPT_EDGE",EDGE,{"disambiguationData":[OSD([sQuery(id+"F0.wireOp",EDGE,"E4.3.0"),subQ0])]}),makeQuery(id+"F1.opExtrude","SWEPT_FACE",FACE,{"disambiguationData":[OSD([subQ0])]})],"blendedInto":[makeQuery(id+"F1.opExtrude","SWEPT_FACE",FACE,{"disambiguationData":[OSD([subQ0])]})]});}
            fillet(context, id + "F3", {"entities" : qUnion([Q0, Q1, Q2, Q3, Q4, Q5, Q6, Q7, Q8, Q9, Q10, Q11, Q12, Q13, Q14, Q15, Q16, Q17, Q18, Q19, Q20, Q21, Q22, Q23, Q24, Q25, Q26, Q27, Q28, Q29, Q30, Q31, Q32, Q33, Q34, Q35, Q36, Q37, Q38, Q39, Q40, Q41]), "radius" : 1 * mm, "tangentPropagation" : true, "allowEdgeOverflow" : false});
        }
    });
